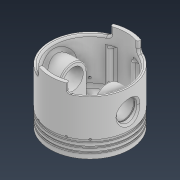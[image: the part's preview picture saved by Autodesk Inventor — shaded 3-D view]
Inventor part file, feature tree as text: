
AUTODESK INVENTOR PART (.ipt)
format: ipt  version: 2022 (Build 260153000, 153)  size: 601,600 bytes
history: native  units: mm
features: sketch x10, extrude x10, plane x8, fillet x5, mirror x3, other x2, projected_geometry x2, hole x1, chamfer x1, pattern_circular x1
ambient origin geometry x8: Origin, YZ Plane, XZ Plane, XY Plane, X Axis, Y Axis, Z Axis, Center Point
bodies: Solid1 (feature_tree)
feature tree (43):
  sketch  "Sketch1"  dims[d0=85.5mm d1=78.0mm]
  extrude  "Extrusion1"  Depth=78.0mm
  extrude  "Extrusion2"  Depth=10.0mm TaperAngle=0.0deg
  plane  "Work Plane1"
  extrude  "Extrusion3"  Depth=10.0mm
  extrude  "Extrusion4"  Depth=2.5mm
  extrude  "Extrusion5"  Depth=40.0mm TaperAngle=0.0deg
  hole  "Hole1"  [1 undecoded]
  other  "Full Round Fillet1"
  other  "Full Round Fillet2"
  fillet  "Fillet1"  Radius=40.0mm
  fillet  "Fillet2"  Radius=15.0mm
  fillet  "Fillet3"  Radius=15.0mm
  fillet  "Fillet4"  Radius=1.0mm
  fillet  "Fillet5"  Radius=3.0mm
  chamfer  "Chamfer1"  Distance=2.0mm Angle=45.0deg
  plane  "Work Plane3"
  plane  "Work Plane4"
  extrude  "Extrusion8"  [1 undecoded]
  plane  "Work Plane5"
  extrude  "Extrusion9"  [1 undecoded]
  plane  "Work Plane6"
  extrude  "Extrusion10"  Depth=1.2mm
  plane  "Work Plane7"
  extrude  "Extrusion11"  Depth=1.2mm TaperAngle=0.0deg
  pattern_circular  "Circular Pattern1"  [2 undecoded]
  mirror  "Mirror2"
  mirror  "Mirror3"
  plane  "Work Plane8"
  extrude  "Extrusion12"  Depth=1.2mm TaperAngle=0.0deg
  mirror  "Mirror4"
  sketch  "Sketch2"  dims[d2=68.0mm d3=0.0mm d4=10.0mm d5=0.0mm]
  sketch  "Sketch3"  dims[d6=10.0mm d7=30.0mm]
  sketch  "Sketch4"  dims[d8=0.0mm d9=0.0mm d10=2.5mm]
  sketch  "Sketch6"  dims[d11=78.0mm d12=40.0mm d13=0.0mm]
  plane  "Work Plane2"
  sketch  "Sketch8"  dims[d14=35.0mm d15=30.0mm d16=40.0mm d17=0.0mm d18=15.0mm d19=15.0mm]
  sketch  "Sketch9"  dims[d20=22.0mm d21=6.0mm d22=4.0mm d23=2.0mm d24=90.0deg d25=8.0mm d26=20.594885mm d27=1.0mm d28=3.0mm]
  sketch  "Sketch10"  dims[d29=3.0mm]
  projected_geometry  "Projected Loop1"
  sketch  "Sketch11"  dims[d30=3.0mm]
  projected_geometry  "Projected Loop2"
  sketch  "Sketch12"  dims[d31=2.0mm d32=2.0mm d33=2.0mm d34=45.0deg d35=-2.0mm d41=-7.0mm d42=83.0mm d43=2.0mm d44=0.0mm d45=-3.0mm d46=2.0mm d47=0.0mm d48=-3.0mm d49=3.0mm d50=0.0mm d51=2.5mm d52=29.25mm d53=6.25mm d54=0.0mm d55=0.0mm d56=20.0mm d57=-4.363323mm d59=36.0mm d60=24.0mm d61=1.2mm d62=0.0mm]
note: 5 required parameter values undecoded (feature->parameter linkage not recoverable at this tier; creation-order binding heuristic only, values carry confidence <= 0.55)
